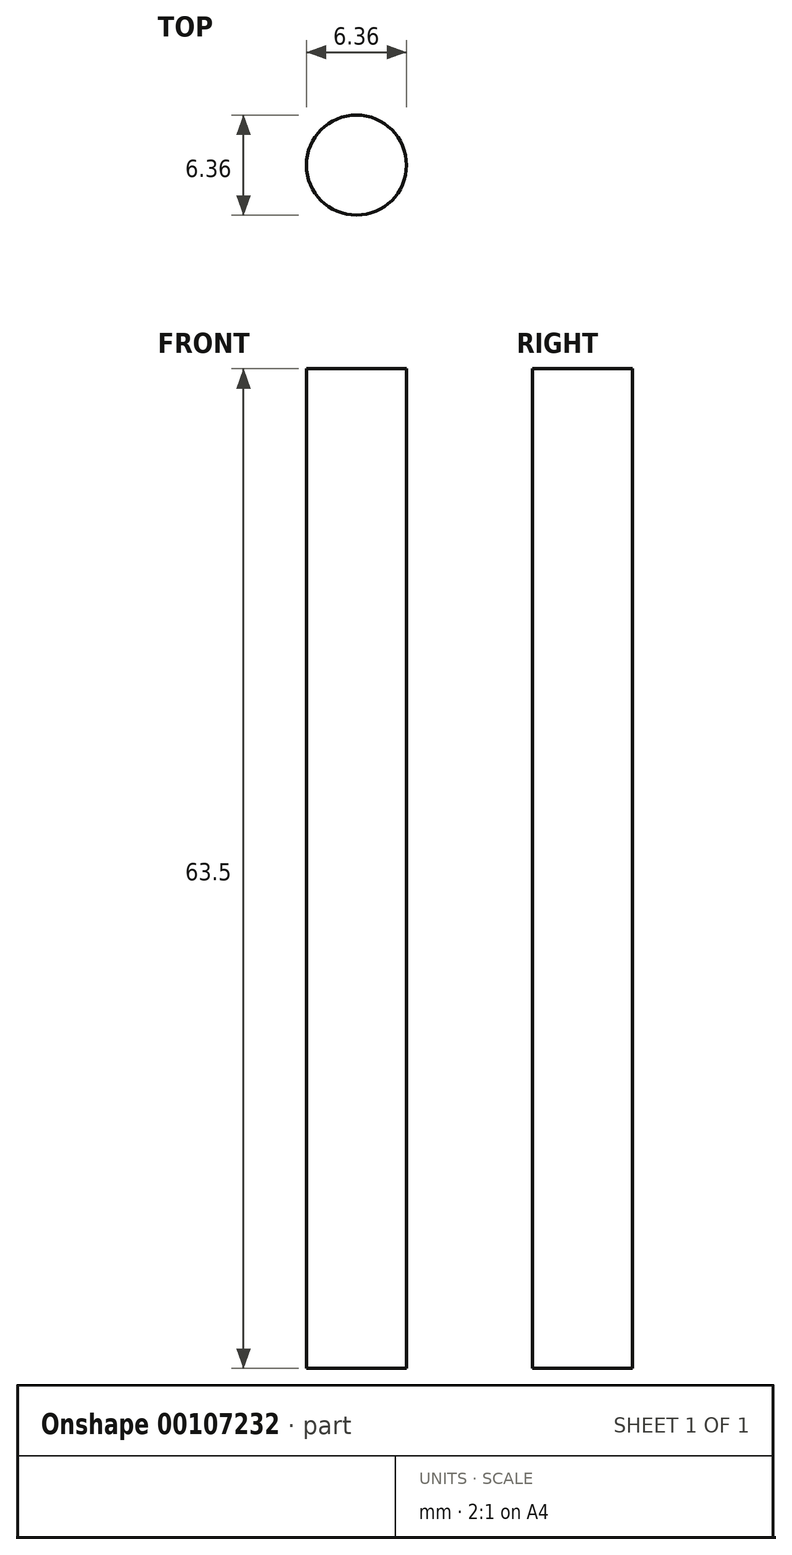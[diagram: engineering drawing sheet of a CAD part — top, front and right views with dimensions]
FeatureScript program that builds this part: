
annotation { "Feature Type Name" : "Feature", "Feature Type Description" : "" }
export const myFeature = defineFeature(function(context is Context, id is Id, definition is map)
    precondition{}
    {
        {
            var Q0;
            Q0=qCreatedBy(makeId("Top.planeOp"),FACE);
            var sketch = newSketch(context, id + "F0", { "sketchPlane" : qUnion([Q0])});
            skCircle(sketch, "E0", {"center": v(0, 0) * mm, "radius": 3.17 * mm});
            skSolve(sketch);
        }
        {
            var Q0;
            Q0=makeQuery(id+"F0.imprint","IMPRINT",FACE,{"disambiguationData":[TD([[makeQuery(id+"F0.imprint","IMPRINT",EDGE,{"derivedFrom":sQuery(id+"F0.wireOp",EDGE,"E0")}),1.0]])]});
            extrude(context, id + "F1", {"entities" : qUnion([Q0]), "depth" : 63.5 * mm});
        }
    });
